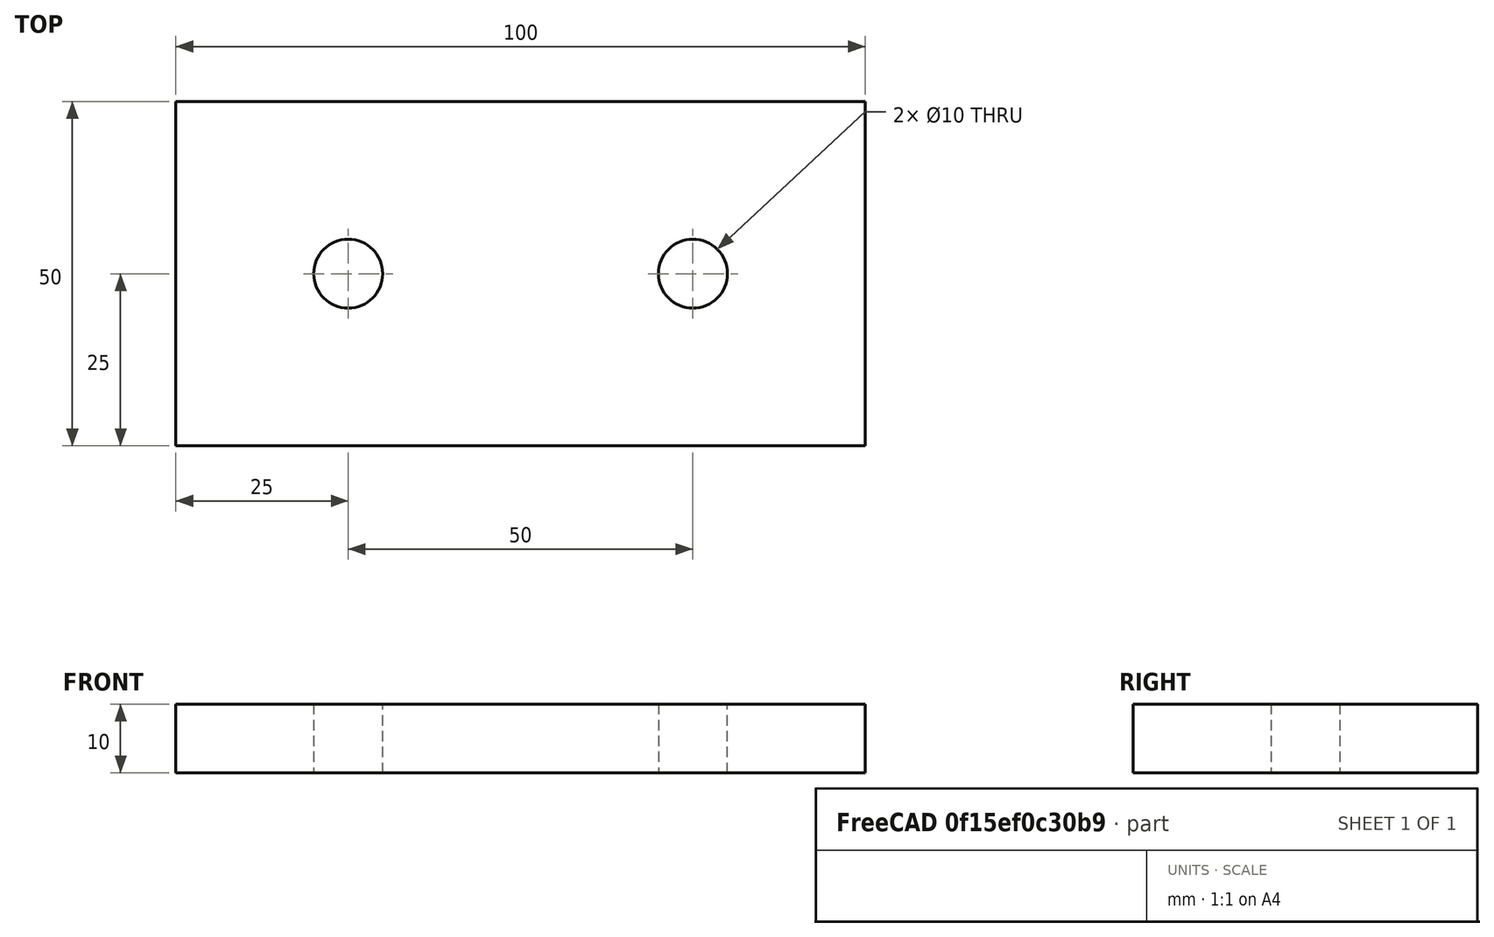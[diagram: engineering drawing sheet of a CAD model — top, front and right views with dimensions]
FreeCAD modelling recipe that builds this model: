
FCSTD DOCUMENT  (FreeCAD 0.21R33668 +26 (Git))
Label: OEM STEP EXPORT
License: All rights reserved
LicenseURL: https://en.wikipedia.org/wiki/All_rights_reserved
objects: TechDraw::DrawViewDimension×8, TechDraw::DrawViewPart×4, Sketcher::SketchObject×1, PartDesign::Pad×1, PartDesign::Body×1, TechDraw::DrawSVGTemplate×1, TechDraw::DrawPage×1
note: 12 computed .brp shape members not serialized (recipe doc carries the construction recipe); baked Part::Feature solids carry a one-line shape summary decoded from their .brp

FEATURE [Sketcher::SketchObject] Sketch
  FullyConstrained = false
  MapMode = 5
  Support = -> [XY_Plane]
  sketch-geometry (6):
    g0: LineSegment StartX=-50.1601 StartY=30.9102 StartZ=0 EndX=49.8399 EndY=30.9102 EndZ=0
    g1: LineSegment StartX=49.8399 StartY=30.9102 StartZ=0 EndX=49.8399 EndY=-19.0898 EndZ=0
    g2: LineSegment StartX=49.8399 StartY=-19.0898 StartZ=0 EndX=-50.1601 EndY=-19.0898 EndZ=0
    g3: LineSegment StartX=-50.1601 StartY=-19.0898 StartZ=0 EndX=-50.1601 EndY=30.9102 EndZ=0
    g4: Circle CenterX=-25.1601 CenterY=5.91022 CenterZ=0 NormalX=0 NormalY=0 NormalZ=1 AngleXU=0 Radius=5
    g5: Circle CenterX=24.8399 CenterY=5.91022 CenterZ=0 NormalX=0 NormalY=0 NormalZ=1 AngleXU=0 Radius=5
  constraints (16):
    c: Coincident(g0,g1)
    c: Coincident(g1,g2)
    c: Coincident(g2,g3)
    c: Coincident(g3,g0)
    c: Horizontal(g0)
    c: Horizontal(g2)
    c: Vertical(g1)
    c: Vertical(g3)
    c: Distance(g0) = 100
    c: Distance(g1) = 50
    c: Diameter(g5) = 10
    c: Diameter(g4) = 10
    c: Distance(g5,g1) = 25
    c: Distance(g4,g3) = 25
    c: Distance(g4,g2) = 25
    c: Distance(g5,g2) = 25
FEATURE [PartDesign::Pad] Pad
  Direction = (0,0,1)
  Length = 10
  Length2 = 10
  Profile = -> Sketch
  ReferenceAxis = -> Sketch [N_Axis]
  Type = 0
FEATURE [PartDesign::Body] Body
  Group = -> [Sketch,Pad]
  Origin = -> Origin
  Tip = -> Pad
FEATURE [TechDraw::DrawSVGTemplate] Template
  EditableTexts = Designed_by_Name=Eng. Kimsh; Drawing_number=A010910; FC-Date=2023.09.10; FC-SC=mm; FC-SH=1 / 1; FC-Title=Title; Subtitle=Simple Plate; Weight=Weight
  Height = 210
  Orientation = 1
  Template = D:/Program Files/FreeCAD 0.21/data/Mod/TechDraw/Templates/A4_LandscapeTD.svg
  Width = 297
FEATURE [TechDraw::DrawViewPart] View  label="Isometric View"
  CoarseView = false
  Direction = (0.57735,-0.57735,0.57735)
  Focus = 100
  HardHidden = false
  IsoCount = 0
  IsoHidden = false
  IsoVisible = false
  LockPosition = false
  Perspective = false
  Rotation = 0
  ScaleType = 0
  ScrubCount = 0
  SeamHidden = false
  SeamVisible = false
  SmoothHidden = false
  SmoothVisible = true
  Source = -> [Pad]
  X = 229.578
  XDirection = (0.707107,0.707107,0)
  Y = 161.237
FEATURE [TechDraw::DrawViewPart] View001  label="Front View"
  CoarseView = false
  Direction = (0,-1,0)
  Focus = 100
  HardHidden = false
  IsoCount = 0
  IsoHidden = false
  IsoVisible = false
  LockPosition = false
  Perspective = false
  Rotation = 0
  ScaleType = 0
  ScrubCount = 0
  SeamHidden = false
  SeamVisible = false
  SmoothHidden = false
  SmoothVisible = true
  Source = -> [Pad]
  X = 67.4219
  XDirection = (1,0,0)
  Y = 39.1025
FEATURE [TechDraw::DrawViewPart] View002  label="Right View"
  CoarseView = false
  Direction = (1,0,0)
  Focus = 100
  HardHidden = false
  IsoCount = 0
  IsoHidden = false
  IsoVisible = false
  LockPosition = false
  Perspective = false
  Rotation = 0
  ScaleType = 0
  ScrubCount = 0
  SeamHidden = false
  SeamVisible = false
  SmoothHidden = false
  SmoothVisible = true
  Source = -> [Pad]
  X = 177.481
  XDirection = (0,1,0)
  Y = 89.4744
FEATURE [TechDraw::DrawViewPart] View003  label="Top View"
  CoarseView = false
  Direction = (0,0,1)
  Focus = 100
  HardHidden = false
  IsoCount = 0
  IsoHidden = false
  IsoVisible = false
  LockPosition = false
  Perspective = false
  Rotation = 0
  ScaleType = 0
  ScrubCount = 0
  SeamHidden = false
  SeamVisible = false
  SmoothHidden = false
  SmoothVisible = true
  Source = -> [Pad]
  X = 66.7319
  XDirection = (1,0,0)
  Y = 89.9437
FEATURE [TechDraw::DrawViewDimension] Dimension
  AngleOverride = false
  Arbitrary = false
  ArbitraryTolerances = false
  EqualTolerance = true
  ExtensionAngle = 0
  FormatSpec = %.2w
  FormatSpecOverTolerance = %+.2w
  FormatSpecUnderTolerance = %+.2w
  Inverted = false
  LineAngle = 0
  LockPosition = false
  MeasureType = 1
  OverTolerance = 0
  References2D = -> [View003]
  Rotation = 0
  ScaleType = 0
  TheoreticalExact = false
  Type = 1
  UnderTolerance = 0
  X = 0.345013
  Y = 45.7857
FEATURE [TechDraw::DrawViewDimension] Dimension001
  AngleOverride = false
  Arbitrary = false
  ArbitraryTolerances = false
  EqualTolerance = true
  ExtensionAngle = 0
  FormatSpec = %.2w
  FormatSpecOverTolerance = %+.2w
  FormatSpecUnderTolerance = %+.2w
  Inverted = false
  LineAngle = 0
  LockPosition = false
  MeasureType = 1
  OverTolerance = 0
  References2D = -> [View003]
  Rotation = 0
  ScaleType = 0
  TheoreticalExact = false
  Type = 2
  UnderTolerance = 0
  X = 55.8652
  Y = 0.774934
FEATURE [TechDraw::DrawViewDimension] Dimension002
  AngleOverride = false
  Arbitrary = false
  ArbitraryTolerances = false
  EqualTolerance = true
  ExtensionAngle = 0
  FormatSpec = %.2w
  FormatSpecOverTolerance = %+.2w
  FormatSpecUnderTolerance = %+.2w
  Inverted = false
  LineAngle = 0
  LockPosition = false
  MeasureType = 1
  OverTolerance = 0
  References2D = -> [View002]
  Rotation = 0
  ScaleType = 0
  TheoreticalExact = false
  Type = 1
  UnderTolerance = 0
  X = -2.41509
  Y = -22.1657
FEATURE [TechDraw::DrawViewDimension] Dimension003
  AngleOverride = false
  Arbitrary = false
  ArbitraryTolerances = false
  EqualTolerance = true
  ExtensionAngle = 0
  FormatSpec = %.2w
  FormatSpecOverTolerance = %+.2w
  FormatSpecUnderTolerance = %+.2w
  Inverted = false
  LineAngle = 0
  LockPosition = false
  MeasureType = 1
  OverTolerance = 0
  References2D = -> [View002]
  Rotation = 0
  ScaleType = 0
  TheoreticalExact = false
  Type = 2
  UnderTolerance = 0
  X = 31.5552
  Y = 2.5
FEATURE [TechDraw::DrawViewDimension] Dimension004
  AngleOverride = false
  Arbitrary = false
  ArbitraryTolerances = false
  EqualTolerance = true
  ExtensionAngle = 0
  FormatSpec = %.2w
  FormatSpecOverTolerance = %+.2w
  FormatSpecUnderTolerance = %+.2w
  Inverted = false
  LineAngle = 0
  LockPosition = false
  MeasureType = 1
  OverTolerance = 0
  References2D = -> [View001]
  Rotation = 0
  ScaleType = 0
  TheoreticalExact = false
  Type = 2
  UnderTolerance = 0
  X = 62.4205
  Y = 2.5
FEATURE [TechDraw::DrawViewDimension] Dimension005
  AngleOverride = false
  Arbitrary = false
  ArbitraryTolerances = false
  EqualTolerance = true
  ExtensionAngle = 0
  FormatSpec = %.2w
  FormatSpecOverTolerance = %+.2w
  FormatSpecUnderTolerance = %+.2w
  Inverted = false
  LineAngle = 0
  LockPosition = false
  MeasureType = 1
  OverTolerance = 0
  References2D = -> [View001]
  Rotation = 0
  ScaleType = 0
  TheoreticalExact = false
  Type = 1
  UnderTolerance = 0
  X = -0.345013
  Y = -18.3706
FEATURE [TechDraw::DrawViewDimension] Dimension006
  AngleOverride = false
  Arbitrary = false
  ArbitraryTolerances = false
  EqualTolerance = true
  ExtensionAngle = 0
  FormatSpec = ⌀%.2w
  FormatSpecOverTolerance = %+.2w
  FormatSpecUnderTolerance = %+.2w
  Inverted = false
  LineAngle = 0
  LockPosition = false
  MeasureType = 1
  OverTolerance = 0
  References2D = -> [View003]
  Rotation = 0
  ScaleType = 0
  TheoreticalExact = false
  Type = 5
  UnderTolerance = 0
  X = 66.7847
  Y = 55.8561
FEATURE [TechDraw::DrawViewDimension] Dimension007
  AngleOverride = false
  Arbitrary = false
  ArbitraryTolerances = false
  EqualTolerance = true
  ExtensionAngle = 0
  FormatSpec = ⌀%.2w
  FormatSpecOverTolerance = %+.2w
  FormatSpecUnderTolerance = %+.2w
  Inverted = false
  LineAngle = 0
  LockPosition = false
  MeasureType = 1
  OverTolerance = 0
  References2D = -> [View003]
  Rotation = 0
  ScaleType = 0
  TheoreticalExact = false
  Type = 5
  UnderTolerance = 0
  X = 26.377
  Y = 61.1466
FEATURE [TechDraw::DrawPage] Page
  KeepUpdated = true
  NextBalloonIndex = 1
  ProjectionType = 0
  Template = -> Template
  Views = -> [View,View001,View002,View003,Dimension,Dimension001,Dimension002,Dimension003,Dimension004,Dimension005,Dimension006,Dimension007]
